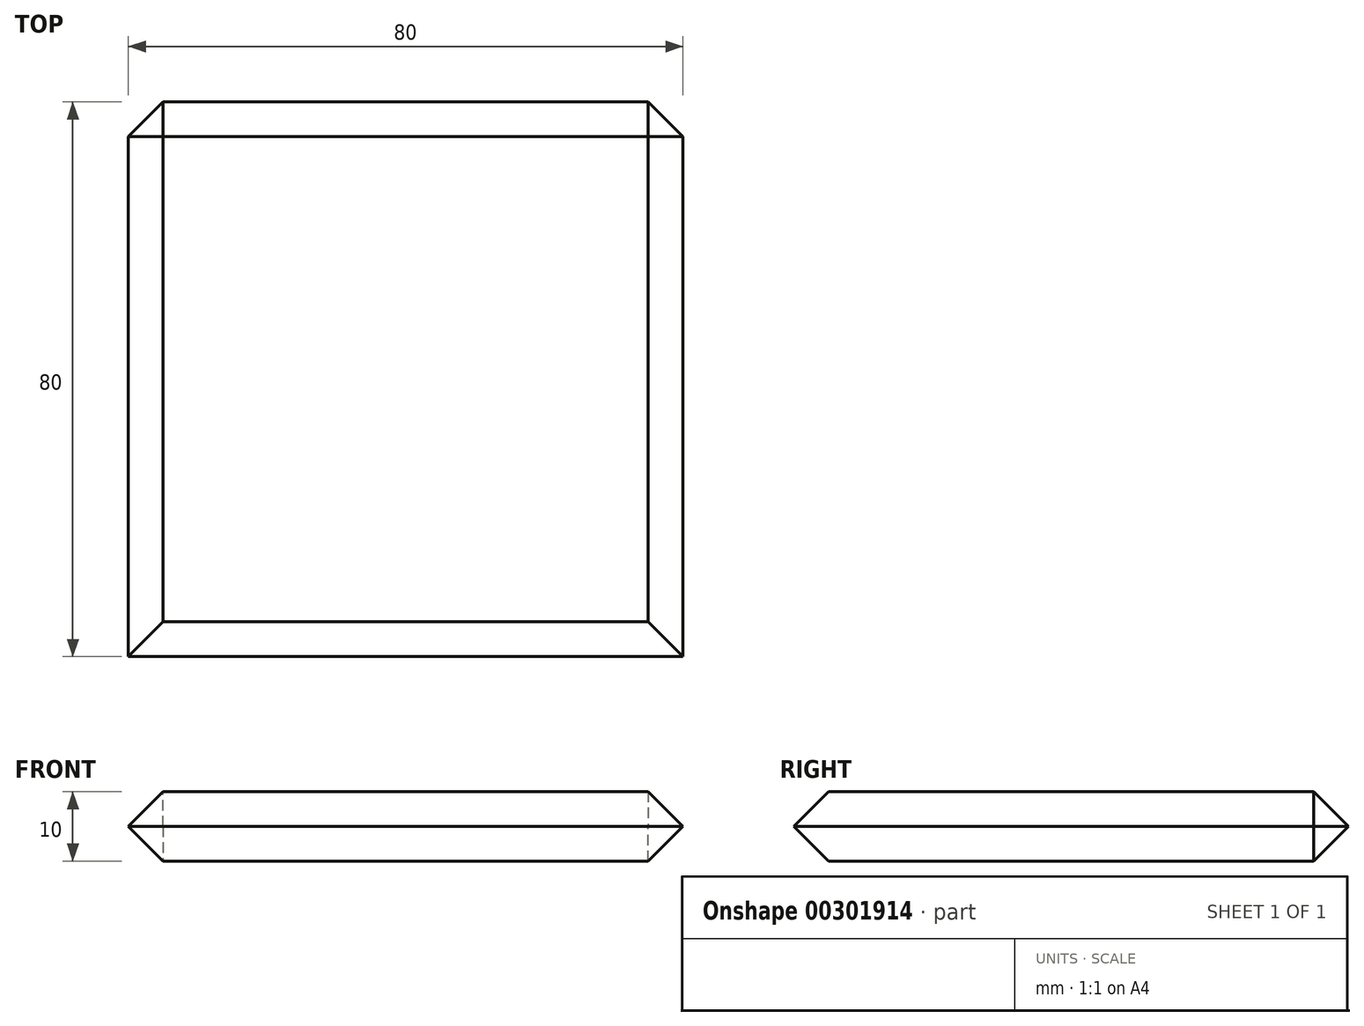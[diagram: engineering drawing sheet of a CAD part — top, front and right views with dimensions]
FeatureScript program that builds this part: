
annotation { "Feature Type Name" : "Feature", "Feature Type Description" : "" }
export const myFeature = defineFeature(function(context is Context, id is Id, definition is map)
    precondition{}
    {
        {
            var Q0;
            Q0=qCreatedBy(makeId("Top.planeOp"),FACE);
            var sketch = newSketch(context, id + "F0", { "sketchPlane" : qUnion([Q0])});
            skLineSegment(sketch, "E0.bottom", {"start": v(0, 0) * mm, "end": v(80, 0) * mm});
            skLineSegment(sketch, "E0.top", {"start": v(0, -80) * mm, "end": v(80, -80) * mm});
            skLineSegment(sketch, "E0.left", {"start": v(0, 0) * mm, "end": v(0, -80) * mm});
            skLineSegment(sketch, "E0.right", {"start": v(80, 0) * mm, "end": v(80, -80) * mm});
            skSolve(sketch);
        }
        {
            var Q0;
            Q0=makeQuery(id+"F0.imprint","IMPRINT",FACE,{"disambiguationData":[TD([[makeQuery(id+"F0.imprint","IMPRINT",EDGE,{"derivedFrom":sQuery(id+"F0.wireOp",EDGE,"E0.bottom")}),-1.0]])]});
            extrude(context, id + "F1", {"entities" : qUnion([Q0]), "depth" : 10 * mm});
        }
        {
            var Q0;
            Q0=makeQuery(id+"F1.opExtrude","CAP_EDGE",EDGE,{"disambiguationData":[OSD([sQuery(id+"F0.wireOp",EDGE,"E0.bottom")])],"isStart":true});
            var Q1;
            Q1=makeQuery(id+"F1.opExtrude","CAP_EDGE",EDGE,{"disambiguationData":[OSD([sQuery(id+"F0.wireOp",EDGE,"E0.bottom")])],"isStart":false});
            var Q2;
            Q2=makeQuery(id+"F1.opExtrude","SWEPT_EDGE",EDGE,{"disambiguationData":[OSD([sQuery(id+"F0.wireOp",EDGE,"E0.bottom"),sQuery(id+"F0.wireOp",EDGE,"E0.left")])]});
            var Q3;
            Q3=makeQuery(id+"F1.opExtrude","SWEPT_EDGE",EDGE,{"disambiguationData":[OSD([sQuery(id+"F0.wireOp",EDGE,"E0.bottom"),sQuery(id+"F0.wireOp",EDGE,"E0.right")])]});
            var Q4;
            Q4=makeQuery(id+"F1.opExtrude","CAP_EDGE",EDGE,{"disambiguationData":[OSD([sQuery(id+"F0.wireOp",EDGE,"E0.right")])],"isStart":true});
            var Q5;
            Q5=makeQuery(id+"F1.opExtrude","CAP_EDGE",EDGE,{"disambiguationData":[OSD([sQuery(id+"F0.wireOp",EDGE,"E0.right")])],"isStart":false});
            var Q6;
            Q6=makeQuery(id+"F1.opExtrude","CAP_EDGE",EDGE,{"disambiguationData":[OSD([sQuery(id+"F0.wireOp",EDGE,"E0.top")])],"isStart":true});
            var Q7;
            Q7=makeQuery(id+"F1.opExtrude","CAP_EDGE",EDGE,{"disambiguationData":[OSD([sQuery(id+"F0.wireOp",EDGE,"E0.top")])],"isStart":false});
            var Q8;
            Q8=makeQuery(id+"F1.opExtrude","CAP_EDGE",EDGE,{"disambiguationData":[OSD([sQuery(id+"F0.wireOp",EDGE,"E0.left")])],"isStart":true});
            var Q9;
            Q9=makeQuery(id+"F1.opExtrude","CAP_EDGE",EDGE,{"disambiguationData":[OSD([sQuery(id+"F0.wireOp",EDGE,"E0.left")])],"isStart":false});
            chamfer(context, id + "F2", {"entities" : qUnion([Q0, Q1, Q2, Q3, Q4, Q5, Q6, Q7, Q8, Q9]), "width" : 5 * mm, "tangentPropagation" : true});
        }
    });
